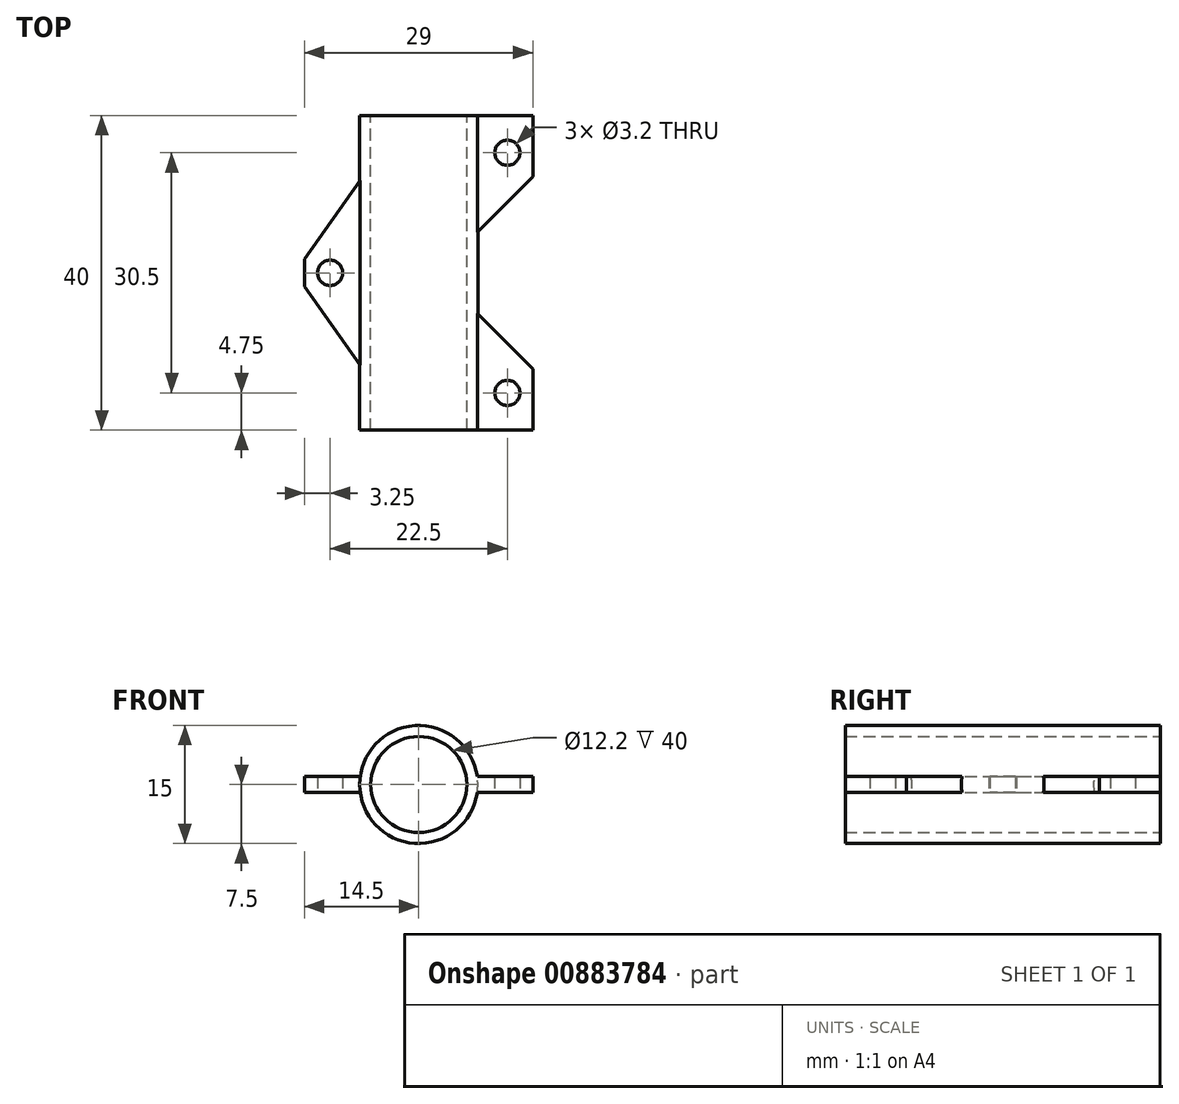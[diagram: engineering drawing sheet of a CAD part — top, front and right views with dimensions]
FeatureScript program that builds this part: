
annotation { "Feature Type Name" : "Feature", "Feature Type Description" : "" }
export const myFeature = defineFeature(function(context is Context, id is Id, definition is map)
    precondition{}
    {
        {
            var Q0;
            Q0=qCreatedBy(makeId("Front.planeOp"),FACE);
            var sketch = newSketch(context, id + "F0", { "sketchPlane" : qUnion([Q0])});
            skCircle(sketch, "E0", {"center": v(0, 0) * mm, "radius": 6.1 * mm});
            skCircle(sketch, "E1.0", {"center": v(0, 0) * mm, "radius": 7.5 * mm});
            skSolve(sketch);
        }
        {
            var Q0;
            Q0=makeQuery(id+"F0.imprint","IMPRINT",FACE,{"disambiguationData":[TD([[makeQuery(id+"F0.imprint","IMPRINT",EDGE,{"derivedFrom":sQuery(id+"F0.wireOp",EDGE,"E0")}),-1.0]])]});
            extrude(context, id + "F1", {"entities" : qUnion([Q0]), "depth" : 40 * mm, "offsetDistance" : 25 * mm});
        }
        {
            var Q0;
            Q0=qCreatedBy(makeId("Top.planeOp"),FACE);
            var sketch = newSketch(context, id + "F2", { "sketchPlane" : qUnion([Q0])});
            skLineSegment(sketch, "E2", {"start": v(6.5, 0) * mm, "end": v(14.5, 0) * mm});
            skLineSegment(sketch, "E3", {"start": v(14.5, 0) * mm, "end": v(14.5, -7.75) * mm});
            skLineSegment(sketch, "E4", {"start": v(14.5, -7.75) * mm, "end": v(6.5, -15.75) * mm});
            skLineSegment(sketch, "E5", {"start": v(6.5, 0) * mm, "end": v(6.5, -15.75) * mm});
            skLineSegment(sketch, "E6", {"start": v(6.5, -40) * mm, "end": v(14.5, -40) * mm});
            skLineSegment(sketch, "E7", {"start": v(14.5, -40) * mm, "end": v(14.5, -32.25) * mm});
            skLineSegment(sketch, "E8", {"start": v(14.5, -32.25) * mm, "end": v(6.5, -24.25) * mm});
            skLineSegment(sketch, "E9", {"start": v(6.5, -24.25) * mm, "end": v(6.5, -40) * mm});
            skLineSegment(sketch, "E10", {"start": v(-6.5, -7) * mm, "end": v(-6.5, -33) * mm});
            skLineSegment(sketch, "E11", {"start": v(-6.5, -33) * mm, "end": v(-14.5, -21.75) * mm});
            skLineSegment(sketch, "E12", {"start": v(-14.5, -21.75) * mm, "end": v(-14.5, -18.25) * mm});
            skLineSegment(sketch, "E13", {"start": v(-14.5, -18.25) * mm, "end": v(-6.5, -7) * mm});
            skLineSegment(sketch, "E14", {"start": v(-16.87, -8.5) * mm, "end": v(0, -8.5) * mm, "construction": true});
            skLineSegment(sketch, "E15", {"start": v(-13.26, -31.5) * mm, "end": v(0, -31.5) * mm, "construction": true});
            skLineSegment(sketch, "E16", {"start": v(-7.5, 1.2) * mm, "end": v(-7.5, -41.91) * mm, "construction": true});
            skLineSegment(sketch, "E17", {"start": v(-19.55, -20) * mm, "end": v(18.62, -20) * mm, "construction": true});
            skCircle(sketch, "E18", {"center": v(-11.25, -20) * mm, "radius": 1.6 * mm});
            skLineSegment(sketch, "E19", {"start": v(1.73, -35.25) * mm, "end": v(21.8, -35.25) * mm, "construction": true});
            skLineSegment(sketch, "E20", {"start": v(1.73, -4.75) * mm, "end": v(21.72, -4.75) * mm, "construction": true});
            skCircle(sketch, "E21", {"center": v(11.25, -35.25) * mm, "radius": 1.6 * mm});
            skCircle(sketch, "E22", {"center": v(11.25, -4.75) * mm, "radius": 1.6 * mm});
            skLineSegment(sketch, "E23", {"start": v(7.5, 1.9) * mm, "end": v(7.5, -41.46) * mm, "construction": true});
            skSolve(sketch);
        }
        {
            var Q0;
            Q0=makeQuery(id+"F2.imprint","IMPRINT",FACE,{"disambiguationData":[TD([[makeQuery(id+"F2.imprint","IMPRINT",EDGE,{"derivedFrom":sQuery(id+"F2.wireOp",EDGE,"E2")}),-1.0]])]});
            var Q1;
            Q1=makeQuery(id+"F2.imprint","IMPRINT",FACE,{"disambiguationData":[TD([[makeQuery(id+"F2.imprint","IMPRINT",EDGE,{"derivedFrom":sQuery(id+"F2.wireOp",EDGE,"E6")}),1.0]])]});
            var Q2;
            Q2=makeQuery(id+"F2.imprint","IMPRINT",FACE,{"disambiguationData":[TD([[makeQuery(id+"F2.imprint","IMPRINT",EDGE,{"derivedFrom":sQuery(id+"F2.wireOp",EDGE,"E10")}),-1.0]])]});
            extrude(context, id + "F3", {"entities" : qUnion([Q0, Q1, Q2]), "operationType" : NewBodyOperationType.ADD, "depth" : 2 * mm, "offsetDistance" : 25 * mm, "symmetric" : true});
        }
    });
